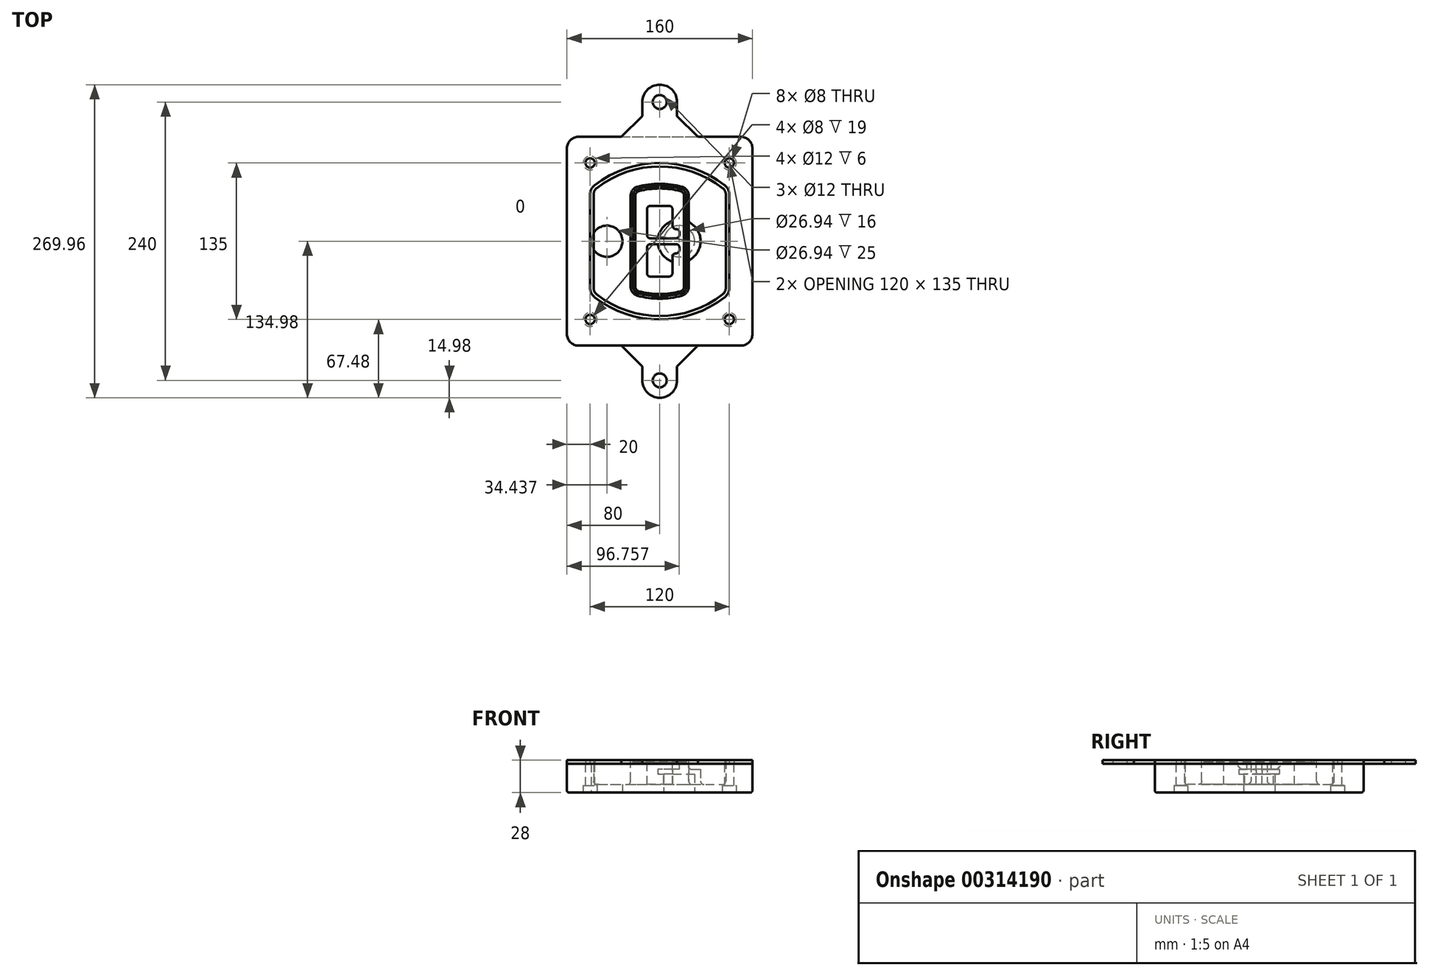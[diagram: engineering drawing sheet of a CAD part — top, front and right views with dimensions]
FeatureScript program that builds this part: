
annotation { "Feature Type Name" : "Feature", "Feature Type Description" : "" }
export const myFeature = defineFeature(function(context is Context, id is Id, definition is map)
    precondition{}
    {
        {
            var Q0;
            Q0=qCreatedBy(makeId("Top.planeOp"),FACE);
            var sketch = newSketch(context, id + "F0", { "sketchPlane" : qUnion([Q0])});
            skPoint(sketch, "E0.rect.middle", {"position": v(0, 0) * mm});
            skLineSegment(sketch, "E1.bottom", {"start": v(-70, -90) * mm, "end": v(70, -90) * mm});
            skLineSegment(sketch, "E1.top", {"start": v(-70, 90) * mm, "end": v(70, 90) * mm});
            skLineSegment(sketch, "E1.left", {"start": v(-80, -80) * mm, "end": v(-80, 80) * mm});
            skLineSegment(sketch, "E1.right", {"start": v(80, -80) * mm, "end": v(80, 80) * mm});
            skLineSegment(sketch, "E2", {"start": v(-80, 90) * mm, "end": v(80, -90) * mm, "construction": true});
            skLineSegment(sketch, "E3", {"start": v(80, 90) * mm, "end": v(-80, -90) * mm, "construction": true});
            skCircle(sketch, "E4", {"center": v(-60, 67.5) * mm, "radius": 4 * mm});
            skCircle(sketch, "E5", {"center": v(60, 67.5) * mm, "radius": 4 * mm});
            skCircle(sketch, "E6", {"center": v(60, -67.5) * mm, "radius": 4 * mm});
            skCircle(sketch, "E7", {"center": v(-60, -67.5) * mm, "radius": 4 * mm});
            skLineSegment(sketch, "E8", {"start": v(-60, 67.5) * mm, "end": v(60, 67.5) * mm, "construction": true});
            skLineSegment(sketch, "E9", {"start": v(60, 67.5) * mm, "end": v(60, -67.5) * mm, "construction": true});
            skLineSegment(sketch, "E10", {"start": v(60, -67.5) * mm, "end": v(-60, -67.5) * mm, "construction": true});
            skLineSegment(sketch, "E11", {"start": v(-60, -67.5) * mm, "end": v(-60, 67.5) * mm, "construction": true});
            skLineSegment(sketch, "E12", {"start": v(-60, 40.3) * mm, "end": v(-60, -40.3) * mm});
            skLineSegment(sketch, "E13", {"start": v(60, 40.3) * mm, "end": v(60, -40.3) * mm});
            skArc(sketch, "E14", {"start": v(56.15, 48.18) * mm, "mid": v(0, 67.5) * mm, "end": v(-56.15, 48.18) * mm});
            skArc(sketch, "E15", {"start": v(-56.15, -48.18) * mm, "mid": v(0, -67.5) * mm, "end": v(56.15, -48.18) * mm});
            skLineSegment(sketch, "E16", {"start": v(-60, 0) * mm, "end": v(60, 0) * mm, "construction": true});
            skPoint(sketch, "E17.visualSharp", {"position": v(-60, -45) * mm});
            skArc(sketch, "E17.filletArc", {"start": v(-60, -40.3) * mm, "mid": v(-58.99, -44.68) * mm, "end": v(-56.15, -48.18) * mm});
            skPoint(sketch, "E18.visualSharp", {"position": v(-60, 45) * mm});
            skArc(sketch, "E18.filletArc", {"start": v(-56.15, 48.18) * mm, "mid": v(-58.99, 44.68) * mm, "end": v(-60, 40.3) * mm});
            skPoint(sketch, "E19.visualSharp", {"position": v(60, 45) * mm});
            skArc(sketch, "E19.filletArc", {"start": v(60, 40.3) * mm, "mid": v(58.99, 44.68) * mm, "end": v(56.15, 48.18) * mm});
            skPoint(sketch, "E20.visualSharp", {"position": v(60, -45) * mm});
            skArc(sketch, "E20.filletArc", {"start": v(56.15, -48.18) * mm, "mid": v(58.99, -44.68) * mm, "end": v(60, -40.3) * mm});
            skPoint(sketch, "E21.visualSharp", {"position": v(-80, 90) * mm});
            skArc(sketch, "E21.filletArc", {"start": v(-70, 90) * mm, "mid": v(-77.07, 87.07) * mm, "end": v(-80, 80) * mm});
            skPoint(sketch, "E22.visualSharp", {"position": v(80, 90) * mm});
            skArc(sketch, "E22.filletArc", {"start": v(80, 80) * mm, "mid": v(77.07, 87.07) * mm, "end": v(70, 90) * mm});
            skPoint(sketch, "E23.visualSharp", {"position": v(80, -90) * mm});
            skArc(sketch, "E23.filletArc", {"start": v(70, -90) * mm, "mid": v(77.07, -87.07) * mm, "end": v(80, -80) * mm});
            skPoint(sketch, "E24.visualSharp", {"position": v(-80, -90) * mm});
            skArc(sketch, "E24.filletArc", {"start": v(-80, -80) * mm, "mid": v(-77.07, -87.07) * mm, "end": v(-70, -90) * mm});
            skArc(sketch, "E25.0", {"start": v(57, 40.3) * mm, "mid": v(56.3, 43.36) * mm, "end": v(54.3, 45.81) * mm});
            skLineSegment(sketch, "E25.1", {"start": v(57, 40.3) * mm, "end": v(57, -40.3) * mm});
            skArc(sketch, "E25.2", {"start": v(54.3, -45.81) * mm, "mid": v(56.3, -43.36) * mm, "end": v(57, -40.3) * mm});
            skArc(sketch, "E25.3", {"start": v(-54.3, -45.81) * mm, "mid": v(0, -64.5) * mm, "end": v(54.3, -45.81) * mm});
            skArc(sketch, "E25.4", {"start": v(-57, -40.3) * mm, "mid": v(-56.3, -43.36) * mm, "end": v(-54.3, -45.81) * mm});
            skArc(sketch, "E25.5", {"start": v(54.3, 45.81) * mm, "mid": v(0, 64.5) * mm, "end": v(-54.3, 45.81) * mm});
            skLineSegment(sketch, "E25.6", {"start": v(-57, 40.3) * mm, "end": v(-57, -40.3) * mm});
            skArc(sketch, "E25.7", {"start": v(-54.3, 45.81) * mm, "mid": v(-56.3, 43.36) * mm, "end": v(-57, 40.3) * mm});
            skArc(sketch, "E26.0", {"start": v(-58.62, 51.33) * mm, "mid": v(-62.58, 46.43) * mm, "end": v(-64, 40.3) * mm});
            skArc(sketch, "E26.1", {"start": v(58.62, 51.33) * mm, "mid": v(0, 71.5) * mm, "end": v(-58.62, 51.33) * mm});
            skArc(sketch, "E26.2", {"start": v(64, 40.3) * mm, "mid": v(62.58, 46.43) * mm, "end": v(58.62, 51.33) * mm});
            skLineSegment(sketch, "E26.3", {"start": v(64, 40.3) * mm, "end": v(64, -40.3) * mm});
            skArc(sketch, "E26.4", {"start": v(58.62, -51.33) * mm, "mid": v(62.58, -46.43) * mm, "end": v(64, -40.3) * mm});
            skLineSegment(sketch, "E26.5", {"start": v(-64, 40.3) * mm, "end": v(-64, -40.3) * mm});
            skArc(sketch, "E26.6", {"start": v(-58.62, -51.33) * mm, "mid": v(0, -71.5) * mm, "end": v(58.62, -51.33) * mm});
            skArc(sketch, "E26.7", {"start": v(-64, -40.3) * mm, "mid": v(-62.58, -46.43) * mm, "end": v(-58.62, -51.33) * mm});
            skSolve(sketch);
        }
        {
            var Q0;
            Q0=makeQuery(id+"F0.imprint","IMPRINT",FACE,{"disambiguationData":[TD([[makeQuery(id+"F0.imprint","IMPRINT",EDGE,{"derivedFrom":sQuery(id+"F0.wireOp",EDGE,"E1.bottom")}),1.0]])]});
            var Q1;
            Q1=makeQuery(id+"F0.imprint","IMPRINT",FACE,{"disambiguationData":[TD([[makeQuery(id+"F0.imprint","IMPRINT",EDGE,{"derivedFrom":sQuery(id+"F0.wireOp",EDGE,"E12")}),1.0]])]});
            var Q2;
            Q2=makeQuery(id+"F0.imprint","IMPRINT",FACE,{"disambiguationData":[TD([[makeQuery(id+"F0.imprint","IMPRINT",EDGE,{"derivedFrom":sQuery(id+"F0.wireOp",EDGE,"E25.0")}),1.0]])]});
            var Q3;
            Q3=makeQuery(id+"F0.imprint","IMPRINT",FACE,{"disambiguationData":[TD([[makeQuery(id+"F0.imprint","IMPRINT",EDGE,{"derivedFrom":sQuery(id+"F0.wireOp",EDGE,"E12")}),-1.0]])]});
            extrude(context, id + "F1", {"entities" : qUnion([Q0, Q1, Q2, Q3]), "oppositeDirection" : true, "depth" : 25 * mm});
        }
        {
            var Q0;
            Q0=makeQuery(id+"F0.imprint","IMPRINT",FACE,{"disambiguationData":[TD([[makeQuery(id+"F0.imprint","IMPRINT",EDGE,{"derivedFrom":sQuery(id+"F0.wireOp",EDGE,"E12")}),1.0]])]});
            extrude(context, id + "F2", {"entities" : qUnion([Q0]), "operationType" : NewBodyOperationType.ADD, "depth" : 3 * mm});
        }
        {
            var Q0;
            Q0=makeQuery(id+"F0.imprint","IMPRINT",FACE,{"disambiguationData":[TD([[makeQuery(id+"F0.imprint","IMPRINT",EDGE,{"derivedFrom":sQuery(id+"F0.wireOp",EDGE,"E25.0")}),1.0]])]});
            extrude(context, id + "F3", {"entities" : qUnion([Q0]), "operationType" : NewBodyOperationType.REMOVE, "oppositeDirection" : true, "depth" : 18 * mm});
        }
        {
            var Q0;
            Q0=makeQuery(id+"F2.opExtrude","CAP_FACE",FACE,{"disambiguationData":[OSD([sQuery(id+"F0.wireOp",EDGE,"E12"),sQuery(id+"F0.wireOp",EDGE,"E13"),sQuery(id+"F0.wireOp",EDGE,"E14"),sQuery(id+"F0.wireOp",EDGE,"E15"),sQuery(id+"F0.wireOp",EDGE,"E17.filletArc"),sQuery(id+"F0.wireOp",EDGE,"E18.filletArc"),sQuery(id+"F0.wireOp",EDGE,"E19.filletArc"),sQuery(id+"F0.wireOp",EDGE,"E20.filletArc"),sQuery(id+"F0.wireOp",EDGE,"E25.0"),sQuery(id+"F0.wireOp",EDGE,"E25.1"),sQuery(id+"F0.wireOp",EDGE,"E25.2"),sQuery(id+"F0.wireOp",EDGE,"E25.3"),sQuery(id+"F0.wireOp",EDGE,"E25.4"),sQuery(id+"F0.wireOp",EDGE,"E25.5"),sQuery(id+"F0.wireOp",EDGE,"E25.6"),sQuery(id+"F0.wireOp",EDGE,"E25.7")])],"isStart":false});
            var sketch = newSketch(context, id + "F4", { "sketchPlane" : qUnion([Q0])});
            skArc(sketch, "E27.0", {"start": v(-19.08, -46.97) * mm, "mid": v(0, -49.5) * mm, "end": v(19.08, -46.97) * mm});
            skArc(sketch, "E28.0", {"start": v(19.08, 46.97) * mm, "mid": v(0, 49.5) * mm, "end": v(-19.08, 46.97) * mm});
            skLineSegment(sketch, "E29", {"start": v(-25, 39.25) * mm, "end": v(-25, -39.25) * mm});
            skLineSegment(sketch, "E30", {"start": v(25, 39.25) * mm, "end": v(25, -39.25) * mm});
            skLineSegment(sketch, "E31", {"start": v(-25, 45.1) * mm, "end": v(25, 45.1) * mm, "construction": true});
            skLineSegment(sketch, "E32", {"start": v(-25, -45.1) * mm, "end": v(25, -45.1) * mm, "construction": true});
            skPoint(sketch, "E33.visualSharp", {"position": v(-25, 45.1) * mm});
            skArc(sketch, "E33.filletArc", {"start": v(-19.08, 46.97) * mm, "mid": v(-23.35, 44.11) * mm, "end": v(-25, 39.25) * mm});
            skPoint(sketch, "E34.visualSharp", {"position": v(25, 45.1) * mm});
            skArc(sketch, "E34.filletArc", {"start": v(25, 39.25) * mm, "mid": v(23.35, 44.11) * mm, "end": v(19.08, 46.97) * mm});
            skPoint(sketch, "E35.visualSharp", {"position": v(25, -45.1) * mm});
            skArc(sketch, "E35.filletArc", {"start": v(19.08, -46.97) * mm, "mid": v(23.35, -44.11) * mm, "end": v(25, -39.25) * mm});
            skPoint(sketch, "E36.visualSharp", {"position": v(-25, -45.1) * mm});
            skArc(sketch, "E36.filletArc", {"start": v(-25, -39.25) * mm, "mid": v(-23.35, -44.11) * mm, "end": v(-19.08, -46.97) * mm});
            skArc(sketch, "E37.0", {"start": v(54.3, 45.81) * mm, "mid": v(0, 64.5) * mm, "end": v(-54.3, 45.81) * mm});
            skArc(sketch, "E37.1", {"start": v(-54.3, 45.81) * mm, "mid": v(-56.3, 43.36) * mm, "end": v(-57, 40.3) * mm});
            skLineSegment(sketch, "E37.2", {"start": v(-57, 40.3) * mm, "end": v(-57, -40.3) * mm});
            skArc(sketch, "E37.3", {"start": v(-57, -40.3) * mm, "mid": v(-56.3, -43.36) * mm, "end": v(-54.3, -45.81) * mm});
            skArc(sketch, "E37.4", {"start": v(-54.3, -45.81) * mm, "mid": v(0, -64.5) * mm, "end": v(54.3, -45.81) * mm});
            skArc(sketch, "E37.5", {"start": v(54.3, -45.81) * mm, "mid": v(56.3, -43.36) * mm, "end": v(57, -40.3) * mm});
            skLineSegment(sketch, "E37.6", {"start": v(57, 40.3) * mm, "end": v(57, -40.3) * mm});
            skArc(sketch, "E37.7", {"start": v(57, 40.3) * mm, "mid": v(56.3, 43.36) * mm, "end": v(54.3, 45.81) * mm});
            skLineSegment(sketch, "E38.0", {"start": v(23, 39.25) * mm, "end": v(23, -39.25) * mm});
            skArc(sketch, "E38.1", {"start": v(18.56, -45.04) * mm, "mid": v(21.76, -42.9) * mm, "end": v(23, -39.25) * mm});
            skArc(sketch, "E38.2", {"start": v(-18.56, -45.04) * mm, "mid": v(0, -47.5) * mm, "end": v(18.56, -45.04) * mm});
            skArc(sketch, "E38.3", {"start": v(-23, -39.25) * mm, "mid": v(-21.76, -42.9) * mm, "end": v(-18.56, -45.04) * mm});
            skLineSegment(sketch, "E38.4", {"start": v(-23, 39.25) * mm, "end": v(-23, -39.25) * mm});
            skArc(sketch, "E38.5", {"start": v(23, 39.25) * mm, "mid": v(21.76, 42.9) * mm, "end": v(18.56, 45.04) * mm});
            skArc(sketch, "E38.6", {"start": v(-18.56, 45.04) * mm, "mid": v(-21.76, 42.9) * mm, "end": v(-23, 39.25) * mm});
            skArc(sketch, "E38.7", {"start": v(18.56, 45.04) * mm, "mid": v(0, 47.5) * mm, "end": v(-18.56, 45.04) * mm});
            skArc(sketch, "E39.0", {"start": v(21, 39.25) * mm, "mid": v(20.18, 41.68) * mm, "end": v(18.04, 43.1) * mm});
            skLineSegment(sketch, "E39.1", {"start": v(21, 39.25) * mm, "end": v(21, -39.25) * mm});
            skArc(sketch, "E39.2", {"start": v(18.04, -43.1) * mm, "mid": v(20.18, -41.68) * mm, "end": v(21, -39.25) * mm});
            skArc(sketch, "E39.3", {"start": v(-18.04, -43.1) * mm, "mid": v(0, -45.5) * mm, "end": v(18.04, -43.1) * mm});
            skArc(sketch, "E39.4", {"start": v(-21, -39.25) * mm, "mid": v(-20.18, -41.68) * mm, "end": v(-18.04, -43.1) * mm});
            skArc(sketch, "E39.5", {"start": v(18.04, 43.1) * mm, "mid": v(0, 45.5) * mm, "end": v(-18.04, 43.1) * mm});
            skLineSegment(sketch, "E39.6", {"start": v(-21, 39.25) * mm, "end": v(-21, -39.25) * mm});
            skArc(sketch, "E39.7", {"start": v(-18.04, 43.1) * mm, "mid": v(-20.18, 41.68) * mm, "end": v(-21, 39.25) * mm});
            skLineSegment(sketch, "E40", {"start": v(-25, 0) * mm, "end": v(25, 0) * mm, "construction": true});
            skLineSegment(sketch, "E41", {"start": v(-11, 5.5) * mm, "end": v(-11, 27.5) * mm});
            skLineSegment(sketch, "E42", {"start": v(-8, 30.5) * mm, "end": v(8, 30.5) * mm});
            skLineSegment(sketch, "E43", {"start": v(11, 27.5) * mm, "end": v(11, 13.5) * mm});
            skLineSegment(sketch, "E44", {"start": v(14, 10.5) * mm, "end": v(14, 10.5) * mm});
            skLineSegment(sketch, "E45", {"start": v(17, 7.5) * mm, "end": v(17, 5.5) * mm});
            skLineSegment(sketch, "E46", {"start": v(14, 2.5) * mm, "end": v(-8, 2.5) * mm});
            skPoint(sketch, "E47.visualSharp", {"position": v(-11, 30.5) * mm});
            skArc(sketch, "E47.filletArc", {"start": v(-8, 30.5) * mm, "mid": v(-10.12, 29.62) * mm, "end": v(-11, 27.5) * mm});
            skPoint(sketch, "E48.visualSharp", {"position": v(11, 30.5) * mm});
            skArc(sketch, "E48.filletArc", {"start": v(11, 27.5) * mm, "mid": v(10.12, 29.62) * mm, "end": v(8, 30.5) * mm});
            skPoint(sketch, "E49.visualSharp", {"position": v(11, 10.5) * mm});
            skArc(sketch, "E49.filletArc", {"start": v(11, 13.5) * mm, "mid": v(11.88, 11.38) * mm, "end": v(14, 10.5) * mm});
            skPoint(sketch, "E50.visualSharp", {"position": v(17, 10.5) * mm});
            skArc(sketch, "E50.filletArc", {"start": v(17, 7.5) * mm, "mid": v(16.12, 9.62) * mm, "end": v(14, 10.5) * mm});
            skPoint(sketch, "E51.visualSharp", {"position": v(17, 2.5) * mm});
            skArc(sketch, "E51.filletArc", {"start": v(14, 2.5) * mm, "mid": v(16.12, 3.38) * mm, "end": v(17, 5.5) * mm});
            skPoint(sketch, "E52.visualSharp", {"position": v(-11, 2.5) * mm});
            skArc(sketch, "E52.filletArc", {"start": v(-11, 5.5) * mm, "mid": v(-10.12, 3.38) * mm, "end": v(-8, 2.5) * mm});
            skLineSegment(sketch, "E53.0.MirrorCS", {"start": v(14, -2.5) * mm, "end": v(-8, -2.5) * mm});
            skArc(sketch, "E54.0.MirrorCS", {"start": v(-11, -5.5) * mm, "mid": v(-10.12, -3.38) * mm, "end": v(-8, -2.5) * mm});
            skLineSegment(sketch, "E55.0.MirrorCS", {"start": v(-11, -5.5) * mm, "end": v(-11, -27.5) * mm});
            skArc(sketch, "E56.0.MirrorCS", {"start": v(-8, -30.5) * mm, "mid": v(-10.12, -29.62) * mm, "end": v(-11, -27.5) * mm});
            skLineSegment(sketch, "E57.0.MirrorCS", {"start": v(-8, -30.5) * mm, "end": v(8, -30.5) * mm});
            skArc(sketch, "E58.0.MirrorCS", {"start": v(11, -27.5) * mm, "mid": v(10.12, -29.62) * mm, "end": v(8, -30.5) * mm});
            skLineSegment(sketch, "E59.0.MirrorCS", {"start": v(11, -27.5) * mm, "end": v(11, -13.5) * mm});
            skArc(sketch, "E60.0.MirrorCS", {"start": v(11, -13.5) * mm, "mid": v(11.88, -11.38) * mm, "end": v(14, -10.5) * mm});
            skArc(sketch, "E61.0.MirrorCS", {"start": v(17, -7.5) * mm, "mid": v(16.12, -9.62) * mm, "end": v(14, -10.5) * mm});
            skLineSegment(sketch, "E62.0.MirrorCS", {"start": v(17, -7.5) * mm, "end": v(17, -5.5) * mm});
            skArc(sketch, "E63.0.MirrorCS", {"start": v(14, -2.5) * mm, "mid": v(16.12, -3.38) * mm, "end": v(17, -5.5) * mm});
            skSolve(sketch);
        }
        {
            var Q0;
            Q0=makeQuery(id+"F4.imprint","IMPRINT",FACE,{"disambiguationData":[TD([[makeQuery(id+"F4.imprint","IMPRINT",EDGE,{"derivedFrom":sQuery(id+"F4.wireOp",EDGE,"E27.0")}),1.0]])]});
            var Q1;
            Q1=makeQuery(id+"F4.imprint","IMPRINT",FACE,{"disambiguationData":[TD([[makeQuery(id+"F4.imprint","IMPRINT",EDGE,{"derivedFrom":sQuery(id+"F4.wireOp",EDGE,"E38.0")}),-1.0]])]});
            var Q2;
            Q2=makeQuery(id+"F4.imprint","IMPRINT",FACE,{"disambiguationData":[TD([[makeQuery(id+"F4.imprint","IMPRINT",EDGE,{"derivedFrom":sQuery(id+"F4.wireOp",EDGE,"E39.0")}),1.0]])]});
            extrude(context, id + "F5", {"entities" : qUnion([Q0, Q1, Q2]), "operationType" : NewBodyOperationType.ADD, "endBound" : BoundingType.UP_TO_NEXT, "oppositeDirection" : true, "depth" : 25 * mm});
        }
        {
            var Q0;
            Q0=makeQuery(id+"F4.imprint","IMPRINT",FACE,{"disambiguationData":[TD([[makeQuery(id+"F4.imprint","IMPRINT",EDGE,{"derivedFrom":sQuery(id+"F4.wireOp",EDGE,"E38.0")}),-1.0]])]});
            extrude(context, id + "F6", {"entities" : qUnion([Q0]), "operationType" : NewBodyOperationType.REMOVE, "oppositeDirection" : true, "depth" : 2 * mm});
        }
        {
            var Q0;
            Q0=makeQuery(id+"F1.opExtrude","CAP_FACE",FACE,{"disambiguationData":[OSD([sQuery(id+"F0.wireOp",EDGE,"E1.bottom"),sQuery(id+"F0.wireOp",EDGE,"E1.top"),sQuery(id+"F0.wireOp",EDGE,"E1.left"),sQuery(id+"F0.wireOp",EDGE,"E1.right"),sQuery(id+"F0.wireOp",EDGE,"E4"),sQuery(id+"F0.wireOp",EDGE,"E5"),sQuery(id+"F0.wireOp",EDGE,"E6"),sQuery(id+"F0.wireOp",EDGE,"E7"),sQuery(id+"F0.wireOp",EDGE,"E21.filletArc"),sQuery(id+"F0.wireOp",EDGE,"E22.filletArc"),sQuery(id+"F0.wireOp",EDGE,"E23.filletArc"),sQuery(id+"F0.wireOp",EDGE,"E24.filletArc")])],"isStart":false});
            var sketch = newSketch(context, id + "F7", { "sketchPlane" : qUnion([Q0])});
            skCircle(sketch, "E64", {"center": v(16.76, 0) * mm, "radius": 13.47 * mm});
            skCircle(sketch, "E65", {"center": v(-45.56, 0) * mm, "radius": 13.47 * mm});
            skLineSegment(sketch, "E66", {"start": v(80, 0) * mm, "end": v(-80, 0) * mm});
            skCircle(sketch, "E67", {"center": v(16.76, 0) * mm, "radius": 18.47 * mm});
            skCircle(sketch, "E68", {"center": v(60, -67.5) * mm, "radius": 6 * mm});
            skCircle(sketch, "E69", {"center": v(-60, -67.5) * mm, "radius": 6 * mm});
            skCircle(sketch, "E70", {"center": v(-60, 67.5) * mm, "radius": 6 * mm});
            skCircle(sketch, "E71", {"center": v(60, 67.5) * mm, "radius": 6 * mm});
            skSolve(sketch);
        }
        {
            var Q0;
            {var subQ1=sQuery(id+"F7.wireOp",EDGE,"E66");var subQ4=sQuery(id+"F7.wireOp",EDGE,"E64");var subQ6=makeQuery(id+"F7.imprint","INTERSECT",VERTEX,{"disambiguationData":[OD(0.0)],"derivedFrom":[subQ4,subQ1]});Q0=makeQuery(id+"F7.imprint","IMPRINT",FACE,{"disambiguationData":[TD([[makeQuery(id+"F7.imprint","IMPRINT",EDGE,{"disambiguationData":[TD([[subQ6,-1.0]])],"derivedFrom":subQ4}),-1.0]])]});}
            var Q1;
            {var subQ0=sQuery(id+"F7.wireOp",EDGE,"E66");var subQ1=sQuery(id+"F7.wireOp",EDGE,"E64");var subQ3=makeQuery(id+"F7.imprint","INTERSECT",VERTEX,{"disambiguationData":[OD(0.0)],"derivedFrom":[subQ1,subQ0]});Q1=makeQuery(id+"F7.imprint","IMPRINT",FACE,{"disambiguationData":[TD([[makeQuery(id+"F7.imprint","IMPRINT",EDGE,{"disambiguationData":[TD([[subQ3,-1.0]])],"derivedFrom":subQ1}),1.0]])]});}
            var Q2;
            {var subQ0=sQuery(id+"F7.wireOp",EDGE,"E66");var subQ1=sQuery(id+"F7.wireOp",EDGE,"E64");var subQ3=makeQuery(id+"F7.imprint","INTERSECT",VERTEX,{"disambiguationData":[OD(0.0)],"derivedFrom":[subQ1,subQ0]});Q2=makeQuery(id+"F7.imprint","IMPRINT",FACE,{"disambiguationData":[TD([[makeQuery(id+"F7.imprint","IMPRINT",EDGE,{"disambiguationData":[TD([[subQ3,1.0]])],"derivedFrom":subQ1}),1.0]])]});}
            var Q3;
            {var subQ1=sQuery(id+"F7.wireOp",EDGE,"E66");var subQ4=sQuery(id+"F7.wireOp",EDGE,"E64");var subQ6=makeQuery(id+"F7.imprint","INTERSECT",VERTEX,{"disambiguationData":[OD(0.0)],"derivedFrom":[subQ4,subQ1]});Q3=makeQuery(id+"F7.imprint","IMPRINT",FACE,{"disambiguationData":[TD([[makeQuery(id+"F7.imprint","IMPRINT",EDGE,{"disambiguationData":[TD([[subQ6,1.0]])],"derivedFrom":subQ4}),-1.0]])]});}
            extrude(context, id + "F8", {"entities" : qUnion([Q0, Q1, Q2, Q3]), "operationType" : NewBodyOperationType.ADD, "oppositeDirection" : true, "depth" : 20 * mm});
        }
        {
            var Q0;
            {var subQ0=sQuery(id+"F7.wireOp",EDGE,"E66");var subQ1=sQuery(id+"F7.wireOp",EDGE,"E64");var subQ3=makeQuery(id+"F7.imprint","INTERSECT",VERTEX,{"disambiguationData":[OD(0.0)],"derivedFrom":[subQ1,subQ0]});Q0=makeQuery(id+"F7.imprint","IMPRINT",FACE,{"disambiguationData":[TD([[makeQuery(id+"F7.imprint","IMPRINT",EDGE,{"disambiguationData":[TD([[subQ3,-1.0]])],"derivedFrom":subQ1}),1.0]])]});}
            var Q1;
            {var subQ0=sQuery(id+"F7.wireOp",EDGE,"E66");var subQ1=sQuery(id+"F7.wireOp",EDGE,"E64");var subQ3=makeQuery(id+"F7.imprint","INTERSECT",VERTEX,{"disambiguationData":[OD(0.0)],"derivedFrom":[subQ1,subQ0]});Q1=makeQuery(id+"F7.imprint","IMPRINT",FACE,{"disambiguationData":[TD([[makeQuery(id+"F7.imprint","IMPRINT",EDGE,{"disambiguationData":[TD([[subQ3,1.0]])],"derivedFrom":subQ1}),1.0]])]});}
            extrude(context, id + "F9", {"entities" : qUnion([Q0, Q1]), "operationType" : NewBodyOperationType.REMOVE, "oppositeDirection" : true, "depth" : 16 * mm});
        }
        {
            var Q0;
            {var subQ0=sQuery(id+"F7.wireOp",EDGE,"E66");var subQ1=sQuery(id+"F7.wireOp",EDGE,"E65");var subQ3=makeQuery(id+"F7.imprint","INTERSECT",VERTEX,{"disambiguationData":[OD(0.0)],"derivedFrom":[subQ1,subQ0]});Q0=makeQuery(id+"F7.imprint","IMPRINT",FACE,{"disambiguationData":[TD([[makeQuery(id+"F7.imprint","IMPRINT",EDGE,{"disambiguationData":[TD([[subQ3,-1.0]])],"derivedFrom":subQ1}),1.0]])]});}
            var Q1;
            {var subQ0=sQuery(id+"F7.wireOp",EDGE,"E66");var subQ1=sQuery(id+"F7.wireOp",EDGE,"E65");var subQ3=makeQuery(id+"F7.imprint","INTERSECT",VERTEX,{"disambiguationData":[OD(0.0)],"derivedFrom":[subQ1,subQ0]});Q1=makeQuery(id+"F7.imprint","IMPRINT",FACE,{"disambiguationData":[TD([[makeQuery(id+"F7.imprint","IMPRINT",EDGE,{"disambiguationData":[TD([[subQ3,1.0]])],"derivedFrom":subQ1}),1.0]])]});}
            extrude(context, id + "F10", {"entities" : qUnion([Q0, Q1]), "operationType" : NewBodyOperationType.REMOVE, "oppositeDirection" : true, "depth" : 25 * mm});
        }
        {
            var Q0;
            Q0=makeQuery(id+"F7.imprint","IMPRINT",FACE,{"disambiguationData":[TD([[makeQuery(id+"F7.imprint","IMPRINT",EDGE,{"derivedFrom":sQuery(id+"F7.wireOp",EDGE,"E68")}),1.0]])]});
            var Q1;
            Q1=makeQuery(id+"F7.imprint","IMPRINT",FACE,{"disambiguationData":[TD([[makeQuery(id+"F7.imprint","IMPRINT",EDGE,{"derivedFrom":makeQuery(id+"F1.opExtrude","CAP_EDGE",EDGE,{"disambiguationData":[OSD([sQuery(id+"F0.wireOp",EDGE,"E5")])],"isStart":false})}),-1.0]])]});
            var Q2;
            Q2=makeQuery(id+"F7.imprint","IMPRINT",FACE,{"disambiguationData":[TD([[makeQuery(id+"F7.imprint","IMPRINT",EDGE,{"derivedFrom":sQuery(id+"F7.wireOp",EDGE,"E69")}),1.0]])]});
            var Q3;
            Q3=makeQuery(id+"F7.imprint","IMPRINT",FACE,{"disambiguationData":[TD([[makeQuery(id+"F7.imprint","IMPRINT",EDGE,{"derivedFrom":makeQuery(id+"F1.opExtrude","CAP_EDGE",EDGE,{"disambiguationData":[OSD([sQuery(id+"F0.wireOp",EDGE,"E4")])],"isStart":false})}),-1.0]])]});
            var Q4;
            Q4=makeQuery(id+"F7.imprint","IMPRINT",FACE,{"disambiguationData":[TD([[makeQuery(id+"F7.imprint","IMPRINT",EDGE,{"derivedFrom":sQuery(id+"F7.wireOp",EDGE,"E70")}),1.0]])]});
            var Q5;
            Q5=makeQuery(id+"F7.imprint","IMPRINT",FACE,{"disambiguationData":[TD([[makeQuery(id+"F7.imprint","IMPRINT",EDGE,{"derivedFrom":makeQuery(id+"F1.opExtrude","CAP_EDGE",EDGE,{"disambiguationData":[OSD([sQuery(id+"F0.wireOp",EDGE,"E7")])],"isStart":false})}),-1.0]])]});
            var Q6;
            Q6=makeQuery(id+"F7.imprint","IMPRINT",FACE,{"disambiguationData":[TD([[makeQuery(id+"F7.imprint","IMPRINT",EDGE,{"derivedFrom":sQuery(id+"F7.wireOp",EDGE,"E71")}),1.0]])]});
            var Q7;
            Q7=makeQuery(id+"F7.imprint","IMPRINT",FACE,{"disambiguationData":[TD([[makeQuery(id+"F7.imprint","IMPRINT",EDGE,{"derivedFrom":makeQuery(id+"F1.opExtrude","CAP_EDGE",EDGE,{"disambiguationData":[OSD([sQuery(id+"F0.wireOp",EDGE,"E6")])],"isStart":false})}),-1.0]])]});
            extrude(context, id + "F11", {"entities" : qUnion([Q0, Q1, Q2, Q3, Q4, Q5, Q6, Q7]), "operationType" : NewBodyOperationType.REMOVE, "oppositeDirection" : true, "depth" : 6 * mm});
        }
        {
            var Q0;
            Q0=makeQuery(id+"F9.boolean.opBoolean","COPY",FACE,{"derivedFrom":makeQuery(id+"F9.opExtrude","CAP_FACE",FACE,{"disambiguationData":[OSD([sQuery(id+"F7.wireOp",EDGE,"E64")])],"isStart":false})});
            var sketch = newSketch(context, id + "F12", { "sketchPlane" : qUnion([Q0])});
            skArc(sketch, "E72.0", {"start": v(11, 17.55) * mm, "mid": v(2.57, 11.82) * mm, "end": v(-1.54, 2.5) * mm});
            skArc(sketch, "E72.1", {"start": v(-1.54, -2.5) * mm, "mid": v(2.57, -11.82) * mm, "end": v(11, -17.55) * mm});
            skLineSegment(sketch, "E73", {"start": v(-1.54, -2.5) * mm, "end": v(14, -2.5) * mm});
            skLineSegment(sketch, "E74.0", {"start": v(14, 2.5) * mm, "end": v(-1.54, 2.5) * mm});
            skArc(sketch, "E74.1", {"start": v(14, 2.5) * mm, "mid": v(16.12, 3.38) * mm, "end": v(17, 5.5) * mm});
            skLineSegment(sketch, "E74.2", {"start": v(17, 7.5) * mm, "end": v(17, 5.5) * mm});
            skArc(sketch, "E74.3", {"start": v(17, 7.5) * mm, "mid": v(16.12, 9.62) * mm, "end": v(14, 10.5) * mm});
            skArc(sketch, "E74.4", {"start": v(11, 13.5) * mm, "mid": v(11.88, 11.38) * mm, "end": v(14, 10.5) * mm});
            skLineSegment(sketch, "E74.5", {"start": v(11, 17.55) * mm, "end": v(11, 13.5) * mm});
            skLineSegment(sketch, "E74.7", {"start": v(14, -2.5) * mm, "end": v(-1.54, -2.5) * mm});
            skArc(sketch, "E74.8", {"start": v(14, -2.5) * mm, "mid": v(16.12, -3.38) * mm, "end": v(17, -5.5) * mm});
            skLineSegment(sketch, "E74.9", {"start": v(17, -7.5) * mm, "end": v(17, -5.5) * mm});
            skArc(sketch, "E74.10", {"start": v(17, -7.5) * mm, "mid": v(16.12, -9.62) * mm, "end": v(14, -10.5) * mm});
            skArc(sketch, "E74.11", {"start": v(11, -13.5) * mm, "mid": v(11.88, -11.38) * mm, "end": v(14, -10.5) * mm});
            skLineSegment(sketch, "E74.12", {"start": v(11, -17.55) * mm, "end": v(11, -13.5) * mm});
            skPoint(sketch, "E75.orphan", {"position": v(11, -27.5) * mm});
            skPoint(sketch, "E76.orphan", {"position": v(-8, -2.5) * mm});
            skPoint(sketch, "E77.orphan", {"position": v(-8, 2.5) * mm});
            skPoint(sketch, "E78.orphan", {"position": v(11, 27.5) * mm});
            skSolve(sketch);
        }
        {
            var Q0;
            {var subQ7=sQuery(id+"F12.wireOp",EDGE,"E72.0");var subQ14=sQuery(id+"F12.wireOp",EDGE,"E72.1");var subQ16=sQuery(id+"F12.wireOp",EDGE,"E74.1");var subQ18=sQuery(id+"F12.wireOp",EDGE,"E74.8");Q0=qUnion([makeQuery(id+"F12.imprint","IMPRINT",FACE,{"disambiguationData":[TD([[makeQuery(id+"F12.imprint","IMPRINT",EDGE,{"derivedFrom":subQ7}),1.0]])]}),makeQuery(id+"F12.imprint","IMPRINT",FACE,{"disambiguationData":[TD([[makeQuery(id+"F12.imprint","IMPRINT",EDGE,{"derivedFrom":subQ14}),1.0]])]}),makeQuery(id+"F12.imprint","IMPRINT",FACE,{"disambiguationData":[TD([[makeQuery(id+"F12.imprint","IMPRINT",EDGE,{"derivedFrom":subQ16}),1.0]])]}),makeQuery(id+"F12.imprint","IMPRINT",FACE,{"disambiguationData":[TD([[makeQuery(id+"F12.imprint","IMPRINT",EDGE,{"derivedFrom":subQ18}),-1.0]])]})]);}
            var Q1;
            Q1=makeQuery(id+"F5.boolean.opBoolean","SPLIT",FACE,{"disambiguationData":[TD([makeQuery(id+"F5.opExtrude","SWEPT_FACE",FACE,{"disambiguationData":[OSD([sQuery(id+"F4.wireOp",EDGE,"E41")])]})])],"derivedFrom":makeQuery(id+"F3.boolean.opBoolean","COPY",FACE,{"derivedFrom":makeQuery(id+"F3.opExtrude","CAP_FACE",FACE,{"disambiguationData":[OSD([sQuery(id+"F0.wireOp",EDGE,"E25.0"),sQuery(id+"F0.wireOp",EDGE,"E25.1"),sQuery(id+"F0.wireOp",EDGE,"E25.2"),sQuery(id+"F0.wireOp",EDGE,"E25.3"),sQuery(id+"F0.wireOp",EDGE,"E25.4"),sQuery(id+"F0.wireOp",EDGE,"E25.5"),sQuery(id+"F0.wireOp",EDGE,"E25.6"),sQuery(id+"F0.wireOp",EDGE,"E25.7")])],"isStart":false})})});
            extrude(context, id + "F13", {"entities" : qUnion([Q0]), "operationType" : NewBodyOperationType.REMOVE, "endBound" : BoundingType.UP_TO_SURFACE, "endBoundEntityFace" : qUnion([Q1]), "depth" : 25 * mm});
        }
        {
            var Q0;
            Q0=makeQuery(id+"F3.boolean.opBoolean","COPY",EDGE,{"derivedFrom":makeQuery(id+"F3.opExtrude","CAP_EDGE",EDGE,{"disambiguationData":[OSD([sQuery(id+"F0.wireOp",EDGE,"E25.6")])],"isStart":false})});
            var Q1;
            Q1=makeQuery(id+"F8.boolean.opBoolean","INTERSECT",EDGE,{"derivedFrom":[makeQuery(id+"F5.opExtrude","SWEPT_FACE",FACE,{"disambiguationData":[OSD([sQuery(id+"F4.wireOp",EDGE,"E30")])]}),makeQuery(id+"F8.opExtrude","CAP_FACE",FACE,{"disambiguationData":[OSD([sQuery(id+"F7.wireOp",EDGE,"E67")])],"isStart":false})]});
            var Q2;
            Q2=makeQuery(id+"F8.boolean.opBoolean","INTERSECT",EDGE,{"disambiguationData":[OD(1.0)],"derivedFrom":[makeQuery(id+"F5.opExtrude","SWEPT_FACE",FACE,{"disambiguationData":[OSD([sQuery(id+"F4.wireOp",EDGE,"E30")])]}),makeQuery(id+"F8.opExtrude","SWEPT_FACE",FACE,{"disambiguationData":[OSD([sQuery(id+"F7.wireOp",EDGE,"E67")])]})]});
            var Q3;
            {var subQ0=sQuery(id+"F4.wireOp",EDGE,"E30");Q3=makeQuery(id+"F8.boolean.opBoolean","SPLIT",EDGE,{"disambiguationData":[TD([makeQuery(id+"F5.opExtrude","SWEPT_FACE",FACE,{"disambiguationData":[OSD([sQuery(id+"F4.wireOp",EDGE,"E35.filletArc")])]})])],"derivedFrom":makeQuery(id+"F5.opExtrude","CAP_EDGE",EDGE,{"disambiguationData":[OSD([subQ0])],"isStart":false})});}
            var Q4;
            {var subQ0=sQuery(id+"F0.wireOp",EDGE,"E25.7");var subQ1=sQuery(id+"F0.wireOp",EDGE,"E25.1");var subQ2=sQuery(id+"F0.wireOp",EDGE,"E25.6");var subQ3=sQuery(id+"F0.wireOp",EDGE,"E25.5");var subQ4=sQuery(id+"F0.wireOp",EDGE,"E25.4");var subQ5=sQuery(id+"F0.wireOp",EDGE,"E25.0");var subQ6=sQuery(id+"F0.wireOp",EDGE,"E25.2");var subQ7=sQuery(id+"F0.wireOp",EDGE,"E25.3");Q4=makeQuery(id+"F8.boolean.opBoolean","INTERSECT",EDGE,{"derivedFrom":[makeQuery(id+"F5.boolean.opBoolean","SPLIT",FACE,{"disambiguationData":[TD([makeQuery(id+"F2.opExtrude","SWEPT_FACE",FACE,{"disambiguationData":[OSD([subQ5])]})])],"derivedFrom":makeQuery(id+"F3.boolean.opBoolean","COPY",FACE,{"derivedFrom":makeQuery(id+"F3.opExtrude","CAP_FACE",FACE,{"disambiguationData":[OSD([subQ5,subQ1,subQ6,subQ7,subQ4,subQ3,subQ2,subQ0])],"isStart":false})})}),makeQuery(id+"F8.opExtrude","SWEPT_FACE",FACE,{"disambiguationData":[OSD([sQuery(id+"F7.wireOp",EDGE,"E67")])]})]});}
            var Q5;
            Q5=makeQuery(id+"F8.boolean.opBoolean","INTERSECT",EDGE,{"disambiguationData":[OD(0.0)],"derivedFrom":[makeQuery(id+"F5.opExtrude","SWEPT_FACE",FACE,{"disambiguationData":[OSD([sQuery(id+"F4.wireOp",EDGE,"E30")])]}),makeQuery(id+"F8.opExtrude","SWEPT_FACE",FACE,{"disambiguationData":[OSD([sQuery(id+"F7.wireOp",EDGE,"E67")])]})]});
            fillet(context, id + "F14", {"entities" : qUnion([Q0, Q1, Q2, Q3, Q4, Q5]), "radius" : 3 * mm, "tangentPropagation" : true, "allowEdgeOverflow" : false});
        }
        {
            var Q0;
            Q0=makeQuery(id+"F1.opExtrude","CAP_EDGE",EDGE,{"disambiguationData":[OSD([sQuery(id+"F0.wireOp",EDGE,"E1.bottom")])],"isStart":false});
            fillet(context, id + "F15", {"entities" : qUnion([Q0]), "radius" : 2 * mm, "tangentPropagation" : true, "allowEdgeOverflow" : false});
        }
        {
            var Q0;
            {var subQ0=sQuery(id+"F0.wireOp",EDGE,"E21.filletArc");var subQ1=sQuery(id+"F0.wireOp",EDGE,"E7");var subQ2=sQuery(id+"F0.wireOp",EDGE,"E6");var subQ3=sQuery(id+"F0.wireOp",EDGE,"E5");var subQ4=sQuery(id+"F0.wireOp",EDGE,"E4");var subQ5=sQuery(id+"F0.wireOp",EDGE,"E22.filletArc");var subQ6=sQuery(id+"F0.wireOp",EDGE,"E1.bottom");var subQ7=sQuery(id+"F0.wireOp",EDGE,"E1.right");var subQ8=sQuery(id+"F0.wireOp",EDGE,"E1.top");var subQ9=sQuery(id+"F0.wireOp",EDGE,"E1.left");var subQ10=sQuery(id+"F0.wireOp",EDGE,"E23.filletArc");var subQ11=sQuery(id+"F0.wireOp",EDGE,"E24.filletArc");Q0=makeQuery(id+"F2.boolean.opBoolean","SPLIT",FACE,{"disambiguationData":[TD([makeQuery(id+"F1.opExtrude","SWEPT_FACE",FACE,{"disambiguationData":[OSD([subQ6])]})])],"derivedFrom":makeQuery(id+"F1.opExtrude","CAP_FACE",FACE,{"disambiguationData":[OSD([subQ6,subQ8,subQ9,subQ7,subQ4,subQ3,subQ2,subQ1,subQ0,subQ5,subQ10,subQ11])],"isStart":true})});}
            var sketch = newSketch(context, id + "F16", { "sketchPlane" : qUnion([Q0])});
            skLineSegment(sketch, "E79", {"start": v(0, 90) * mm, "end": v(0, 120) * mm, "construction": true});
            skPoint(sketch, "E79.endSnap0", {"position": v(0, 90) * mm});
            skCircle(sketch, "E80", {"center": v(0, 120) * mm, "radius": 6 * mm});
            skLineSegment(sketch, "E81", {"start": v(0, 120) * mm, "end": v(-15, 120) * mm, "construction": true});
            skLineSegment(sketch, "E82", {"start": v(0, 120) * mm, "end": v(15, 120) * mm, "construction": true});
            skArc(sketch, "E83", {"start": v(15, 120) * mm, "mid": v(0, 134.98) * mm, "end": v(-15, 120) * mm});
            skLineSegment(sketch, "E84", {"start": v(-15, 120) * mm, "end": v(-15, 108) * mm});
            skLineSegment(sketch, "E85", {"start": v(15, 120) * mm, "end": v(15.01, 108) * mm});
            skLineSegment(sketch, "E86", {"start": v(-33, 90) * mm, "end": v(-15, 108) * mm});
            skLineSegment(sketch, "E87", {"start": v(33.01, 90) * mm, "end": v(15.01, 108) * mm});
            skLineSegment(sketch, "E88", {"start": v(-80, 0) * mm, "end": v(80, 0) * mm, "construction": true});
            skLineSegment(sketch, "E89.MirrorCS", {"start": v(-33, -90) * mm, "end": v(-15, -108) * mm});
            skLineSegment(sketch, "E90.MirrorCS", {"start": v(-15, -120) * mm, "end": v(-15, -108) * mm});
            skLineSegment(sketch, "E91.MirrorCS", {"start": v(33.01, -90) * mm, "end": v(15.01, -108) * mm});
            skLineSegment(sketch, "E92.MirrorCS", {"start": v(15, -120) * mm, "end": v(15.01, -108) * mm});
            skArc(sketch, "E93.MirrorCS", {"start": v(15, -120) * mm, "mid": v(0, -134.98) * mm, "end": v(-15, -120) * mm});
            skCircle(sketch, "E94.MirrorC", {"center": v(0, -120) * mm, "radius": 6 * mm});
            skLineSegment(sketch, "E95.MirrorCS", {"start": v(0, -90) * mm, "end": v(0, -120) * mm, "construction": true});
            skSolve(sketch);
        }
        {
            var Q0;
            Q0=makeQuery(id+"F16.imprint","IMPRINT",FACE,{"disambiguationData":[TD([[makeQuery(id+"F16.imprint","IMPRINT",EDGE,{"derivedFrom":sQuery(id+"F16.wireOp",EDGE,"E80")}),-1.0]])]});
            var Q1;
            {var subQ1=sQuery(id+"F16.wireOp",EDGE,"E89.MirrorCS");Q1=makeQuery(id+"F16.imprint","IMPRINT",FACE,{"disambiguationData":[TD([[makeQuery(id+"F16.imprint","IMPRINT",EDGE,{"derivedFrom":subQ1}),1.0]])]});}
            var Q2;
            Q2=makeQuery(id+"F16.imprint","IMPRINT",FACE,{"disambiguationData":[TD([[makeQuery(id+"F16.imprint","IMPRINT",EDGE,{"derivedFrom":makeQuery(id+"F1.opExtrude","CAP_EDGE",EDGE,{"disambiguationData":[OSD([sQuery(id+"F0.wireOp",EDGE,"E1.left")])],"isStart":true})}),-1.0]])]});
            var Q3;
            Q3=makeQuery(id+"F2.opExtrude","CAP_FACE",FACE,{"disambiguationData":[OSD([sQuery(id+"F0.wireOp",EDGE,"E12"),sQuery(id+"F0.wireOp",EDGE,"E13"),sQuery(id+"F0.wireOp",EDGE,"E14"),sQuery(id+"F0.wireOp",EDGE,"E15"),sQuery(id+"F0.wireOp",EDGE,"E17.filletArc"),sQuery(id+"F0.wireOp",EDGE,"E18.filletArc"),sQuery(id+"F0.wireOp",EDGE,"E19.filletArc"),sQuery(id+"F0.wireOp",EDGE,"E20.filletArc"),sQuery(id+"F0.wireOp",EDGE,"E25.0"),sQuery(id+"F0.wireOp",EDGE,"E25.1"),sQuery(id+"F0.wireOp",EDGE,"E25.2"),sQuery(id+"F0.wireOp",EDGE,"E25.3"),sQuery(id+"F0.wireOp",EDGE,"E25.4"),sQuery(id+"F0.wireOp",EDGE,"E25.5"),sQuery(id+"F0.wireOp",EDGE,"E25.6"),sQuery(id+"F0.wireOp",EDGE,"E25.7")])],"isStart":false});
            extrude(context, id + "F17", {"entities" : qUnion([Q0, Q1, Q2]), "endBound" : BoundingType.UP_TO_SURFACE, "endBoundEntityFace" : qUnion([Q3]), "depth" : 25 * mm});
        }
        {
            var Q0;
            {var subQ0=sQuery(id+"F16.wireOp",EDGE,"9b71217f-5ebf-48da-81dc-f2ab91c205831.MirrorCS");Q0=makeQuery(id+"F16.imprint","IMPRINT",FACE,{"disambiguationData":[TD([[makeQuery(id+"F16.imprint","IMPRINT",EDGE,{"derivedFrom":subQ0}),1.0]])]});}
            var Q1;
            Q1=makeQuery(id+"F16.imprint","IMPRINT",FACE,{"disambiguationData":[TD([[makeQuery(id+"F16.imprint","IMPRINT",EDGE,{"derivedFrom":sQuery(id+"F16.wireOp",EDGE,"E80")}),-1.0]])]});
            var Q2;
            Q2=makeQuery(id+"F16.imprint","IMPRINT",FACE,{"disambiguationData":[TD([[makeQuery(id+"F16.imprint","IMPRINT",EDGE,{"derivedFrom":makeQuery(id+"F1.opExtrude","CAP_EDGE",EDGE,{"disambiguationData":[OSD([sQuery(id+"F0.wireOp",EDGE,"E1.left")])],"isStart":true})}),-1.0]])]});
            var Q3;
            Q3=makeQuery(id+"F2.opExtrude","CAP_FACE",FACE,{"disambiguationData":[OSD([sQuery(id+"F0.wireOp",EDGE,"E12"),sQuery(id+"F0.wireOp",EDGE,"E13"),sQuery(id+"F0.wireOp",EDGE,"E14"),sQuery(id+"F0.wireOp",EDGE,"E15"),sQuery(id+"F0.wireOp",EDGE,"E17.filletArc"),sQuery(id+"F0.wireOp",EDGE,"E18.filletArc"),sQuery(id+"F0.wireOp",EDGE,"E19.filletArc"),sQuery(id+"F0.wireOp",EDGE,"E20.filletArc"),sQuery(id+"F0.wireOp",EDGE,"E25.0"),sQuery(id+"F0.wireOp",EDGE,"E25.1"),sQuery(id+"F0.wireOp",EDGE,"E25.2"),sQuery(id+"F0.wireOp",EDGE,"E25.3"),sQuery(id+"F0.wireOp",EDGE,"E25.4"),sQuery(id+"F0.wireOp",EDGE,"E25.5"),sQuery(id+"F0.wireOp",EDGE,"E25.6"),sQuery(id+"F0.wireOp",EDGE,"E25.7")])],"isStart":false});
            extrude(context, id + "F18", {"entities" : qUnion([Q0, Q1, Q2]), "endBound" : BoundingType.UP_TO_SURFACE, "endBoundEntityFace" : qUnion([Q3]), "depth" : 25 * mm});
        }
    });
